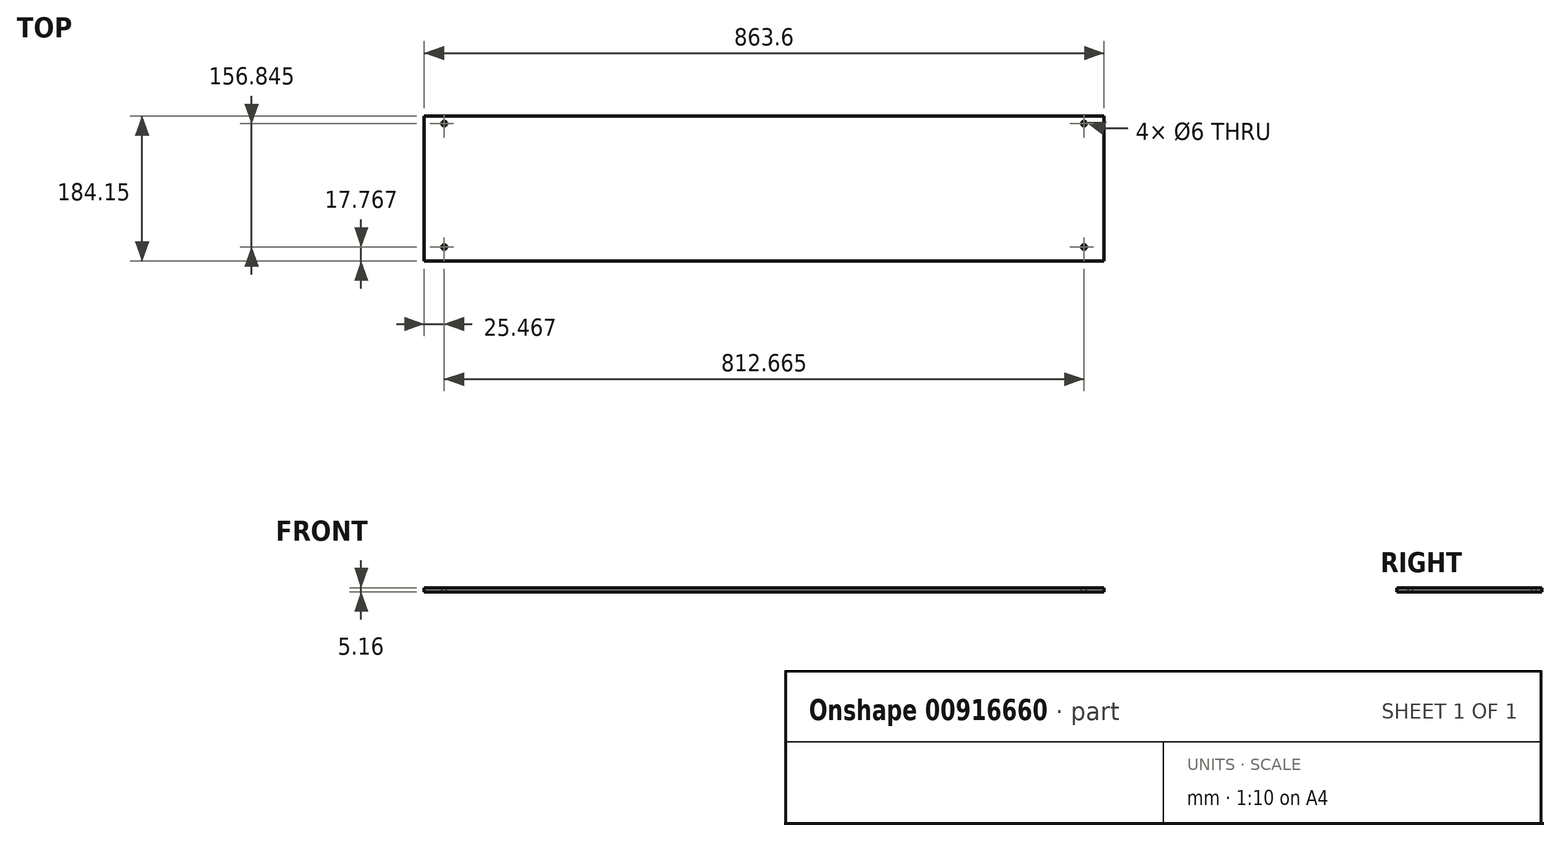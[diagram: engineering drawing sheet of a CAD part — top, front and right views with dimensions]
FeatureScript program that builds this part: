
annotation { "Feature Type Name" : "Feature", "Feature Type Description" : "" }
export const myFeature = defineFeature(function(context is Context, id is Id, definition is map)
    precondition{}
    {
        {
            var Q0;
            Q0=qCreatedBy(makeId("Top.planeOp"),FACE);
            var sketch = newSketch(context, id + "F0", { "sketchPlane" : qUnion([Q0])});
            skLineSegment(sketch, "E0", {"start": v(0, 0) * mm, "end": v(0, -184.15) * mm});
            skLineSegment(sketch, "E1", {"start": v(0, -184.15) * mm, "end": v(863.6, -184.15) * mm});
            skLineSegment(sketch, "E2", {"start": v(863.6, -184.15) * mm, "end": v(863.6, 0) * mm});
            skLineSegment(sketch, "E3", {"start": v(863.6, 0) * mm, "end": v(0, 0) * mm});
            skSolve(sketch);
        }
        {
            var Q0;
            Q0 = qSketchRegion(id + "F0", true);
            extrude(context, id + "F1", {"entities" : qUnion([Q0]), "depth" : 5.16 * mm, "offsetDistance" : 25.4 * mm});
        }
        {
            var Q0;
            Q0=makeQuery(id+"F1.opExtrude","CAP_FACE",FACE,{"disambiguationData":[OSD([sQuery(id+"F0.wireOp",EDGE,"E0"),sQuery(id+"F0.wireOp",EDGE,"E1"),sQuery(id+"F0.wireOp",EDGE,"E2"),sQuery(id+"F0.wireOp",EDGE,"E3")])],"isStart":false});
            var sketch = newSketch(context, id + "F2", { "sketchPlane" : qUnion([Q0])});
            skPoint(sketch, "E4", {"position": v(25.47, -9.54) * mm});
            skPoint(sketch, "E5", {"position": v(838.13, -9.54) * mm});
            skPoint(sketch, "E6", {"position": v(25.47, -166.38) * mm});
            skPoint(sketch, "E7", {"position": v(838.13, -166.38) * mm});
            skSolve(sketch);
        }
        {
            var Q0;
            Q0=sQuery(id+"F2.wireOp",VERTEX,"E4");
            var Q1;
            Q1=sQuery(id+"F2.wireOp",VERTEX,"E6");
            var Q2;
            Q2=sQuery(id+"F2.wireOp",VERTEX,"E7");
            var Q3;
            Q3=sQuery(id+"F2.wireOp",VERTEX,"E5");
            var Q4;
            Q4=makeQuery(id+"F1.opExtrude","SWEPT_BODY",BODY,{"disambiguationData":[OSD([sQuery(id+"F0.wireOp",EDGE,"E0"),sQuery(id+"F0.wireOp",EDGE,"E1"),sQuery(id+"F0.wireOp",EDGE,"E2"),sQuery(id+"F0.wireOp",EDGE,"E3")])]});
            hole(context, id + "F3", {"style" : HoleStyle.SIMPLE, "endStyle" : HoleEndStyle.THROUGH, "holeDiameter" : 6 * mm, "majorDiameter" : 6.35 * mm, "isTappedThrough" : true, "tappedDepth" : 12.7 * mm, "tapClearance" : 3, "locations" : qUnion([Q0, Q1, Q2, Q3]), "scope" : qUnion([Q4])});
        }
    });
